# Revit family: REVIT-PVIFX-2017
name_source: partatom
category: Mechanical Equipment
revit_build: Autodesk Revit 2017 (Build: 20190507_1515(x64)
units: mm (PartAtom-declared; Revit-internal decimal feet)

## family parameters
Always vertical = Yes
Cut with Voids When Loaded = No
Part Type = Normal
Room Calculation Point = No
Round Connector Dimension = Use Radius
Shared = No
Work Plane-Based = No

## types (6) — shared parameters
Air Inlet Diameter = 6"
Air Inlet Radius = 3"
Apparent Load = 1800 VA
Assembly Code = D3020100
Building Return NPT = 2"
Building Return Radius = 1"
Cold Inlet Extension = 16 3/8"
Cold Inlet Height = 6"
Cold Inlet NPT = 2 1/2"
Cold Inlet Radius = 1 1/4"
Condensate Connection = 3/4"
Condensate Connection Extension = 43"
Condensate Connection Radius = 3/8"
Control Panel Extension = 29 1/2"
Current = 15 A
Description = PowerVT Plus Water Heater
Disclaimer = This rendering is for building modeling purposes only. Submittal/catalog is still the contract document. PVI reserves the right to change design and specification without notice.
Drain Extension = 26 3/8"
Drain Height = 21 7/8"
Drain NPT = 1"
Drain Radius = 1/2"
Front Skid = 22 1/2"
Gas Inlet NPT = 1 1/2"
Gas Inlet Radius = 3/4"
Hot Outlet Extension = 27"
Hot Outlet NPT = 2"
Hot Outlet Radius = 1"
Manufacturer = PVI Industries, LLC
Recirculation Height = 22 1/2"
Relief Extension = 23 1/2"
Relief NPT = 1"
Relief Radius = 1/2"
Skid Length = 64"
Skid Spacing = 24 1/2"
URL = www.pvi.com
Unit Radius = 22 1/2"
Vent Angle = 0.00°
Vent Diameter = 6 5/8"
Vent Extension = 38 3/16"
Vent Height = 7"
Vent Radius = 3 5/16"

## per-type parameters (varying)
| type | Burner Conn Height | Hot Outlet Height | Input | Recovery Rate 40F to 140F (gph) | Relief Height | Unit Height | Weight |
| 150 LX 250A-PVIF | 64" | 56" | 1500000 Btu/h | 1737 | 56" | 68" | 2115 |
| 180 LX 250A-PVIF | 64" | 56" | 1800000 Btu/h | 2085 | 56" | 68" | 2115 |
| 200 LX 250A-PVIF | 64" | 56" | 2000000 Btu/h | 2317 | 56" | 68" | 2115 |
| 150 LX 300A-PVIF | 76" | 67" | 1500000 Btu/h | 1737 | 68" | 80" | 2280 |
| 180 LX 300A-PVIF | 76" | 67" | 1800000 Btu/h | 2085 | 68" | 80" | 2280 |
| 200 LX 300A-PVIF | 76" | 67" | 2000000 Btu/h | 2317 | 68" | 80" | 2280 |

note: column(s) folded — value = type name in every type: Model

## geometry (parser evidence)
native form markers: Blend x2, Sweep x2
no freeform markers — native parametric forms only
